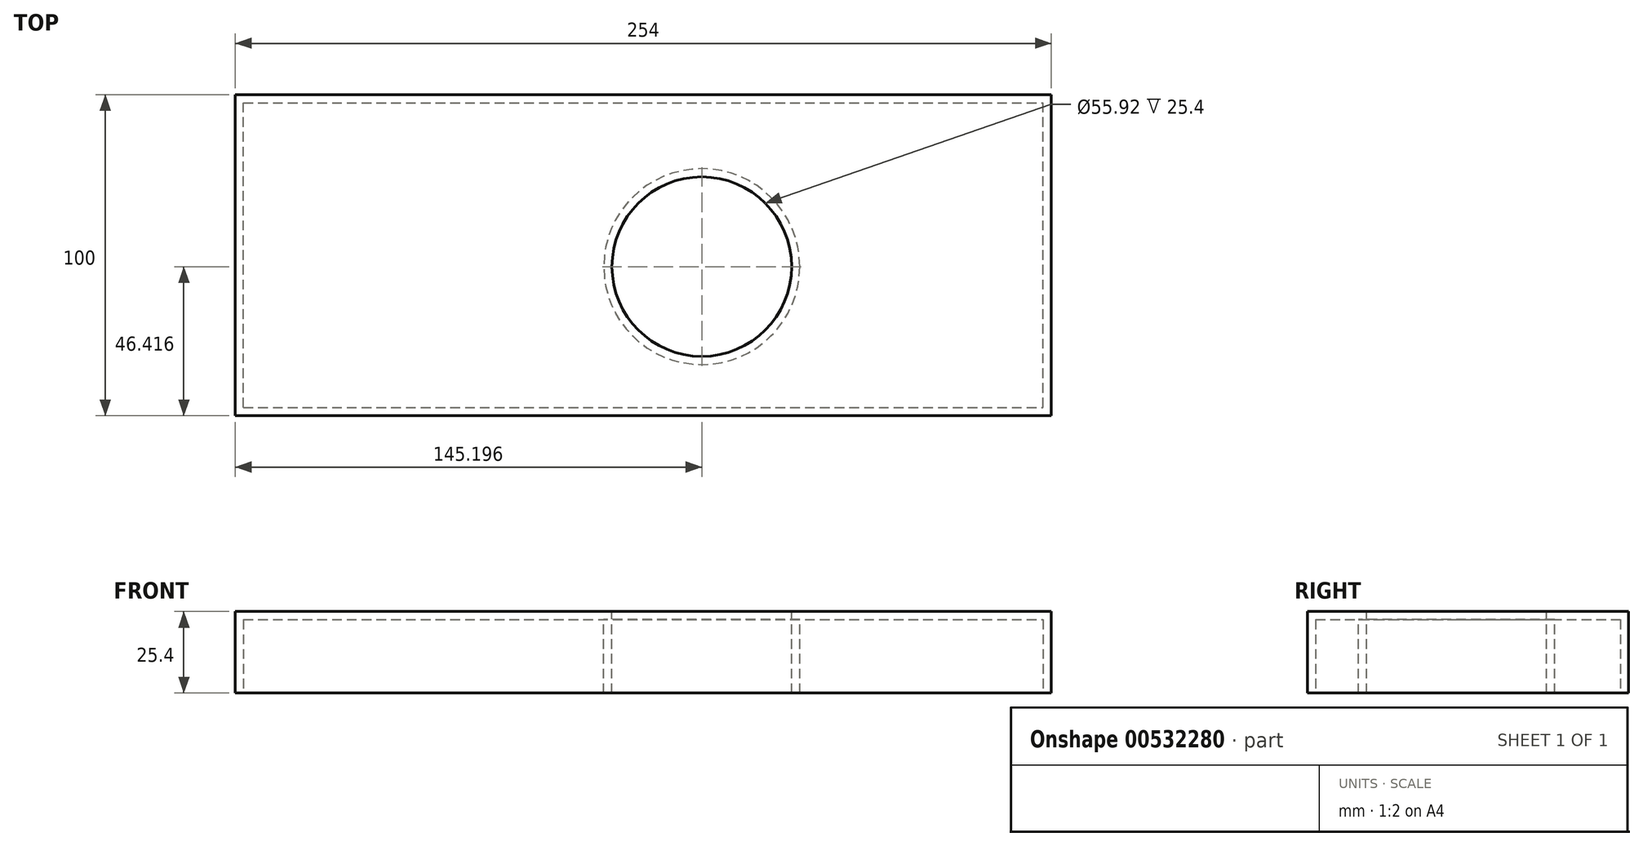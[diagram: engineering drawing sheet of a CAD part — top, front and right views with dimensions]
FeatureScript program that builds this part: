
annotation { "Feature Type Name" : "Feature", "Feature Type Description" : "" }
export const myFeature = defineFeature(function(context is Context, id is Id, definition is map)
    precondition{}
    {
        {
            var Q0;
            Q0=qCreatedBy(makeId("Top.planeOp"),FACE);
            var sketch = newSketch(context, id + "F0", { "sketchPlane" : qUnion([Q0])});
            skLineSegment(sketch, "E0.bottom", {"start": v(0, 0) * mm, "end": v(254, 0) * mm});
            skLineSegment(sketch, "E0.top", {"start": v(0, 100) * mm, "end": v(254, 100) * mm});
            skLineSegment(sketch, "E0.left", {"start": v(0, 0) * mm, "end": v(0, 100) * mm});
            skLineSegment(sketch, "E0.right", {"start": v(254, 0) * mm, "end": v(254, 100) * mm});
            skSolve(sketch);
        }
        {
            var Q0;
            Q0=makeQuery(id+"F0.imprint","IMPRINT",FACE,{"disambiguationData":[TD([[makeQuery(id+"F0.imprint","IMPRINT",EDGE,{"derivedFrom":sQuery(id+"F0.wireOp",EDGE,"E0.bottom")}),1.0]])]});
            extrude(context, id + "F1", {"entities" : qUnion([Q0]), "depth" : 25.4 * mm, "offsetDistance" : 25.4 * mm});
        }
        {
            var Q0;
            Q0=makeQuery(id+"F1.opExtrude","CAP_FACE",FACE,{"disambiguationData":[OSD([sQuery(id+"F0.wireOp",EDGE,"E0.bottom"),sQuery(id+"F0.wireOp",EDGE,"E0.top"),sQuery(id+"F0.wireOp",EDGE,"E0.left"),sQuery(id+"F0.wireOp",EDGE,"E0.right")])],"isStart":false});
            var sketch = newSketch(context, id + "F2", { "sketchPlane" : qUnion([Q0])});
            skCircle(sketch, "E1", {"center": v(145.2, 46.42) * mm, "radius": 27.96 * mm});
            skSolve(sketch);
        }
        {
            var Q0;
            Q0=makeQuery(id+"F2.imprint","IMPRINT",FACE,{"disambiguationData":[TD([[makeQuery(id+"F2.imprint","IMPRINT",EDGE,{"derivedFrom":sQuery(id+"F2.wireOp",EDGE,"E1")}),-1.0]])]});
            extrude(context, id + "F3", {"entities" : qUnion([Q0]), "operationType" : NewBodyOperationType.INTERSECT, "oppositeDirection" : true, "depth" : 25.4 * mm, "offsetDistance" : 25.4 * mm});
        }
        {
            var Q0;
            Q0=makeQuery(id+"F1.opExtrude","CAP_FACE",FACE,{"disambiguationData":[OSD([sQuery(id+"F0.wireOp",EDGE,"E0.bottom"),sQuery(id+"F0.wireOp",EDGE,"E0.top"),sQuery(id+"F0.wireOp",EDGE,"E0.left"),sQuery(id+"F0.wireOp",EDGE,"E0.right")])],"isStart":true});
            shell(context, id + "F4", {"entities" : qUnion([Q0]), "thickness" : 2.54 * mm});
        }
    });
